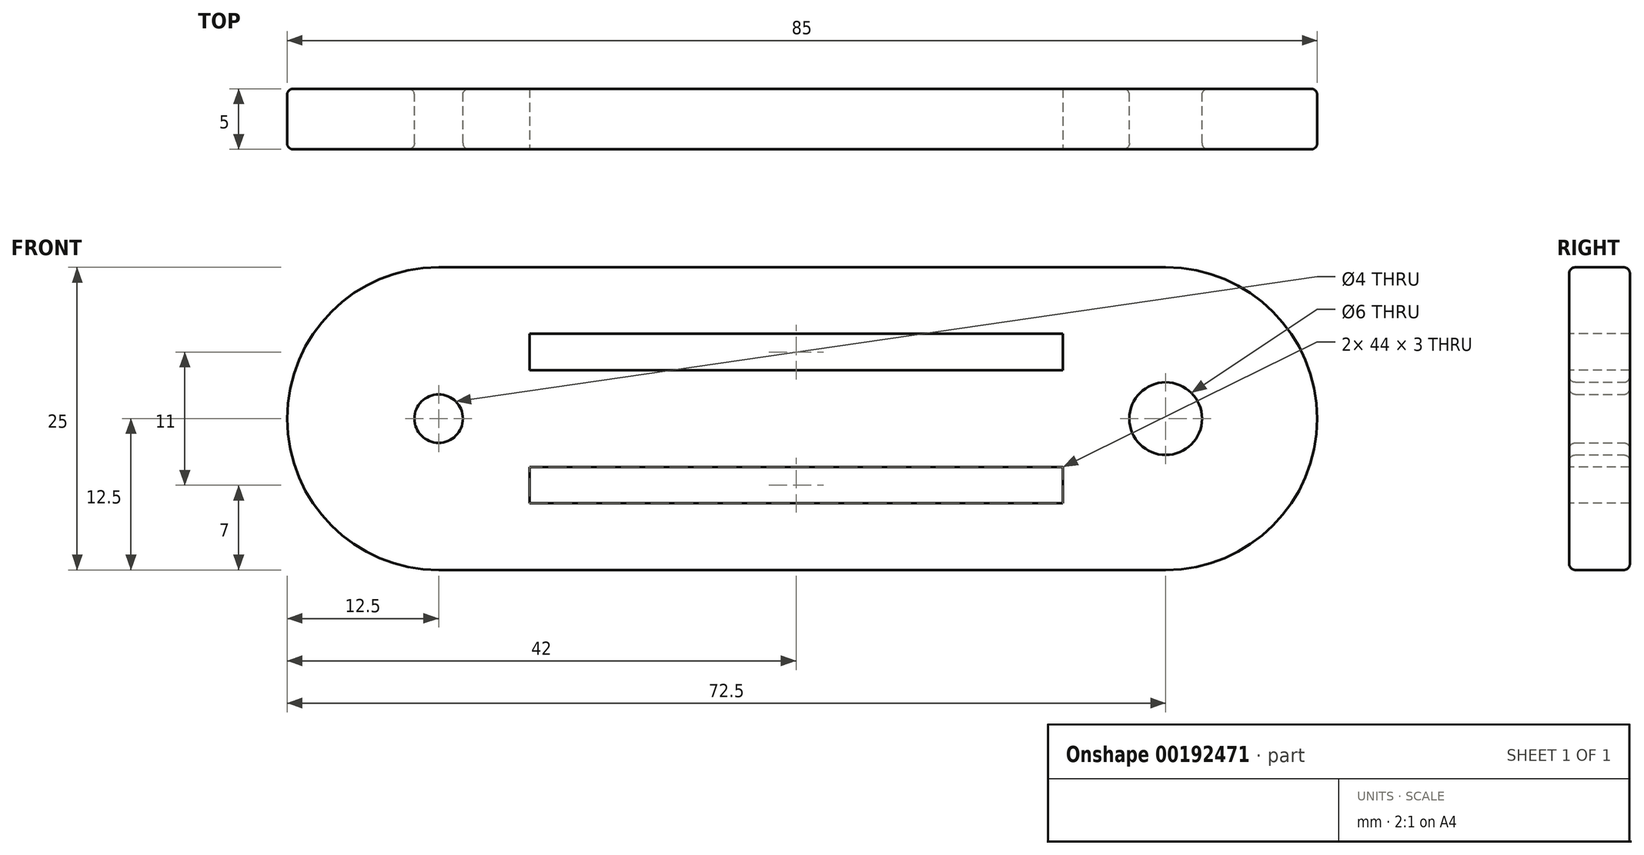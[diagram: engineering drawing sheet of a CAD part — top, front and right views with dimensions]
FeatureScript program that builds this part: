
annotation { "Feature Type Name" : "Feature", "Feature Type Description" : "" }
export const myFeature = defineFeature(function(context is Context, id is Id, definition is map)
    precondition{}
    {
        {
            var Q0;
            Q0=qCreatedBy(makeId("Front.planeOp"),FACE);
            var sketch = newSketch(context, id + "F0", { "sketchPlane" : qUnion([Q0])});
            skLineSegment(sketch, "E0", {"start": v(0, 0) * mm, "end": v(-30, 0) * mm});
            skLineSegment(sketch, "E1", {"start": v(0, 0) * mm, "end": v(30, 0) * mm});
            skCircle(sketch, "E2", {"center": v(-30, 0) * mm, "radius": 20 * mm, "construction": true});
            skCircle(sketch, "E3", {"center": v(30, 0) * mm, "radius": 20 * mm, "construction": true});
            skCircle(sketch, "E4", {"center": v(-30, 0) * mm, "radius": 12.5 * mm});
            skCircle(sketch, "E5", {"center": v(30, 0) * mm, "radius": 12.5 * mm});
            skCircle(sketch, "E6", {"center": v(30, 0) * mm, "radius": 5 * mm, "construction": true});
            skCircle(sketch, "E7", {"center": v(-30, 0) * mm, "radius": 5 * mm, "construction": true});
            skLineSegment(sketch, "E8", {"start": v(-30, -12.5) * mm, "end": v(30, -12.5) * mm});
            skLineSegment(sketch, "E9", {"start": v(30, 12.5) * mm, "end": v(-30, 12.5) * mm});
            skCircle(sketch, "E10", {"center": v(-30, 0) * mm, "radius": 2 * mm});
            skCircle(sketch, "E11", {"center": v(30, 0) * mm, "radius": 3 * mm});
            skSolve(sketch);
        }
        {
            var Q0;
            {var subQ5=sQuery(id+"F0.wireOp",EDGE,"E9");Q0=makeQuery(id+"F0.imprint","IMPRINT",FACE,{"disambiguationData":[TD([[makeQuery(id+"F0.imprint","IMPRINT",EDGE,{"derivedFrom":subQ5}),1.0]])]});}
            var Q1;
            {var subQ0=sQuery(id+"F0.wireOp",EDGE,"E8");Q1=makeQuery(id+"F0.imprint","IMPRINT",FACE,{"disambiguationData":[TD([[makeQuery(id+"F0.imprint","IMPRINT",EDGE,{"derivedFrom":subQ0}),1.0]])]});}
            var Q2;
            Q2=makeQuery(id+"F0.imprint","IMPRINT",FACE,{"disambiguationData":[TD([[makeQuery(id+"F0.imprint","IMPRINT",EDGE,{"derivedFrom":sQuery(id+"F0.wireOp",EDGE,"E11")}),-1.0]])]});
            var Q3;
            Q3=makeQuery(id+"F0.imprint","IMPRINT",FACE,{"disambiguationData":[TD([[makeQuery(id+"F0.imprint","IMPRINT",EDGE,{"derivedFrom":sQuery(id+"F0.wireOp",EDGE,"E10")}),-1.0]])]});
            extrude(context, id + "F1", {"entities" : qUnion([Q0, Q1, Q2, Q3]), "depth" : 5 * mm});
        }
        {
            var Q0;
            Q0=makeQuery(id+"F1.opExtrude","CAP_FACE",FACE,{"disambiguationData":[OSD([sQuery(id+"F0.wireOp",EDGE,"E4"),sQuery(id+"F0.wireOp",EDGE,"E5"),sQuery(id+"F0.wireOp",EDGE,"E8"),sQuery(id+"F0.wireOp",EDGE,"E9"),sQuery(id+"F0.wireOp",EDGE,"E10"),sQuery(id+"F0.wireOp",EDGE,"E11")])],"isStart":false});
            var Q1;
            Q1=makeQuery(id+"F1.opExtrude","CAP_FACE",FACE,{"disambiguationData":[OSD([sQuery(id+"F0.wireOp",EDGE,"E4"),sQuery(id+"F0.wireOp",EDGE,"E5"),sQuery(id+"F0.wireOp",EDGE,"E8"),sQuery(id+"F0.wireOp",EDGE,"E9"),sQuery(id+"F0.wireOp",EDGE,"E10"),sQuery(id+"F0.wireOp",EDGE,"E11")])],"isStart":true});
            fillet(context, id + "F2", {"entities" : qUnion([Q0, Q1]), "radius" : 0.5 * mm, "tangentPropagation" : true, "allowEdgeOverflow" : false});
        }
        {
            var Q0;
            Q0=makeQuery(id+"F1.opExtrude","CAP_FACE",FACE,{"disambiguationData":[OSD([sQuery(id+"F0.wireOp",EDGE,"E4"),sQuery(id+"F0.wireOp",EDGE,"E5"),sQuery(id+"F0.wireOp",EDGE,"E8"),sQuery(id+"F0.wireOp",EDGE,"E9"),sQuery(id+"F0.wireOp",EDGE,"E10"),sQuery(id+"F0.wireOp",EDGE,"E11")])],"isStart":false});
            var sketch = newSketch(context, id + "F3", { "sketchPlane" : qUnion([Q0])});
            skLineSegment(sketch, "E12", {"start": v(0, 0) * mm, "end": v(0, 7) * mm, "construction": true});
            skLineSegment(sketch, "E13.bottom", {"start": v(-22.5, 7) * mm, "end": v(21.5, 7) * mm});
            skLineSegment(sketch, "E13.top", {"start": v(-22.5, -7) * mm, "end": v(21.5, -7) * mm});
            skLineSegment(sketch, "E13.left", {"start": v(-22.5, 7) * mm, "end": v(-22.5, -7) * mm});
            skLineSegment(sketch, "E13.right", {"start": v(21.5, 7) * mm, "end": v(21.5, -7) * mm});
            skLineSegment(sketch, "E14.top", {"start": v(-22.5, 4) * mm, "end": v(21.5, 4) * mm});
            skLineSegment(sketch, "E14.left", {"start": v(-22.5, 7) * mm, "end": v(-22.5, 4) * mm});
            skLineSegment(sketch, "E14.right", {"start": v(21.5, 7) * mm, "end": v(21.5, 4) * mm});
            skLineSegment(sketch, "E15.top", {"start": v(-22.5, -4) * mm, "end": v(21.5, -4) * mm});
            skLineSegment(sketch, "E15.left", {"start": v(-22.5, -7) * mm, "end": v(-22.5, -4) * mm});
            skLineSegment(sketch, "E15.right", {"start": v(21.5, -7) * mm, "end": v(21.5, -4) * mm});
            skArc(sketch, "E16", {"start": v(-22.5, -4) * mm, "mid": v(-24, -5.5) * mm, "end": v(-22.5, -7) * mm});
            skArc(sketch, "E17", {"start": v(-22.5, 4) * mm, "mid": v(-24, 5.5) * mm, "end": v(-22.5, 7) * mm});
            skArc(sketch, "E18", {"start": v(21.5, 7) * mm, "mid": v(23, 5.5) * mm, "end": v(21.5, 4) * mm});
            skArc(sketch, "E19", {"start": v(21.5, -4) * mm, "mid": v(23, -5.5) * mm, "end": v(21.5, -7) * mm});
            skSolve(sketch);
        }
        {
            var Q0;
            Q0=makeQuery(id+"F3.imprint","IMPRINT",FACE,{"disambiguationData":[TD([[makeQuery(id+"F3.imprint","IMPRINT",EDGE,{"derivedFrom":sQuery(id+"F3.wireOp",EDGE,"E13.bottom")}),-1.0]])]});
            var Q1;
            Q1=makeQuery(id+"F3.imprint","IMPRINT",FACE,{"disambiguationData":[TD([[makeQuery(id+"F3.imprint","IMPRINT",EDGE,{"derivedFrom":sQuery(id+"F3.wireOp",EDGE,"E14.left")}),-1.0]])]});
            var Q2;
            Q2=makeQuery(id+"F3.imprint","IMPRINT",FACE,{"disambiguationData":[TD([[makeQuery(id+"F3.imprint","IMPRINT",EDGE,{"derivedFrom":sQuery(id+"F3.wireOp",EDGE,"E14.right")}),1.0]])]});
            var Q3;
            Q3=makeQuery(id+"F3.imprint","IMPRINT",FACE,{"disambiguationData":[TD([[makeQuery(id+"F3.imprint","IMPRINT",EDGE,{"derivedFrom":sQuery(id+"F3.wireOp",EDGE,"E15.right")}),-1.0]])]});
            var Q4;
            Q4=makeQuery(id+"F3.imprint","IMPRINT",FACE,{"disambiguationData":[TD([[makeQuery(id+"F3.imprint","IMPRINT",EDGE,{"derivedFrom":sQuery(id+"F3.wireOp",EDGE,"E13.top")}),1.0]])]});
            var Q5;
            Q5=makeQuery(id+"F3.imprint","IMPRINT",FACE,{"disambiguationData":[TD([[makeQuery(id+"F3.imprint","IMPRINT",EDGE,{"derivedFrom":sQuery(id+"F3.wireOp",EDGE,"E15.left")}),1.0]])]});
            extrude(context, id + "F4", {"entities" : qUnion([Q0, Q1, Q2, Q3, Q4, Q5]), "operationType" : NewBodyOperationType.REMOVE, "endBound" : BoundingType.THROUGH_ALL, "oppositeDirection" : true, "depth" : 25 * mm});
        }
    });
